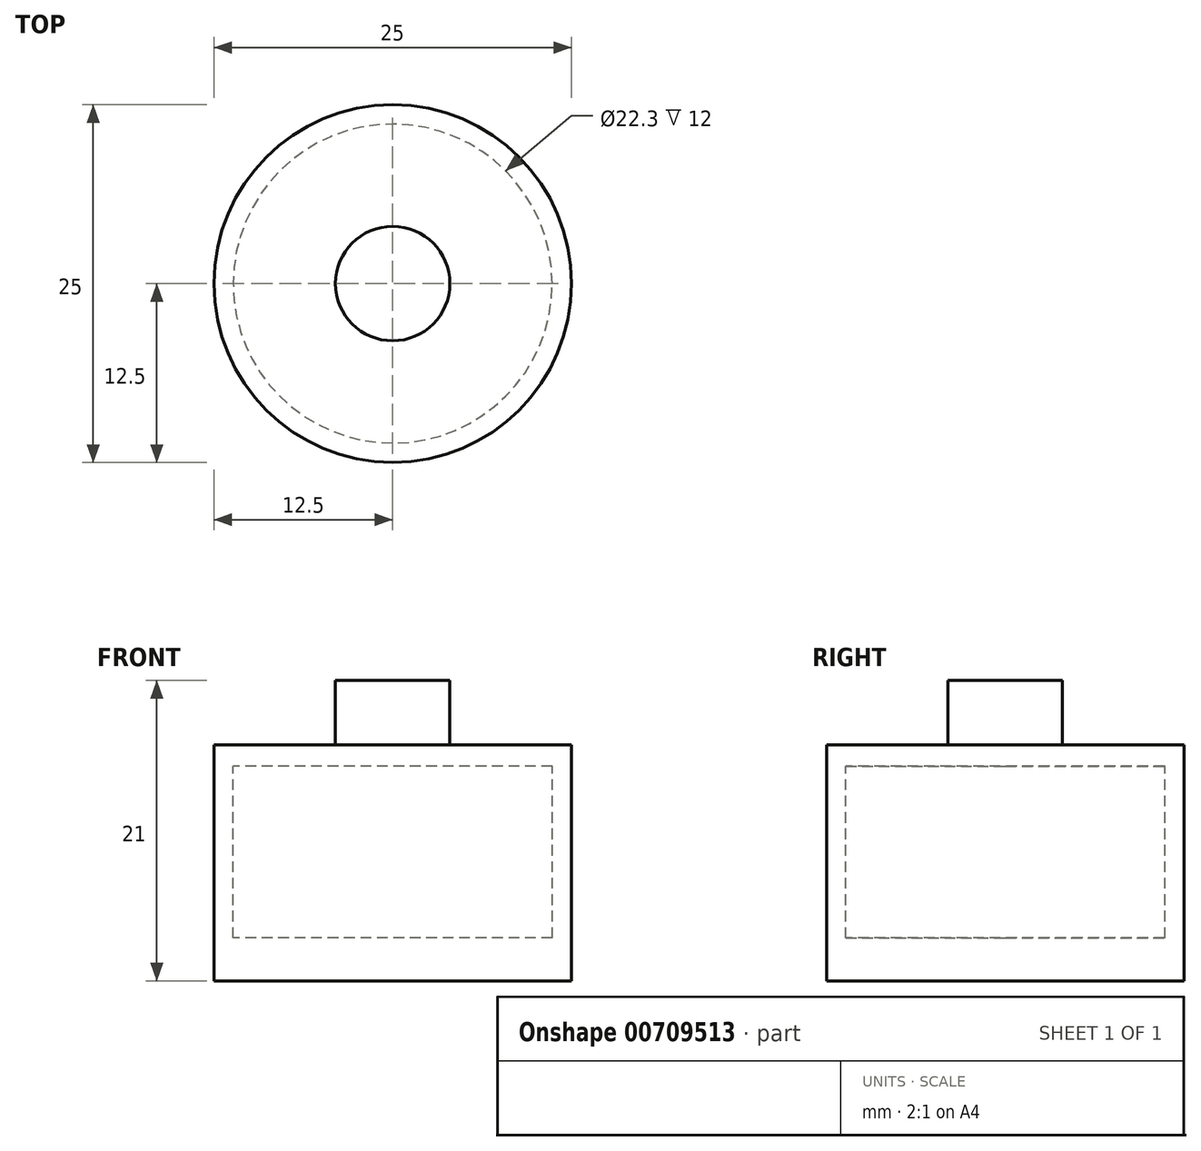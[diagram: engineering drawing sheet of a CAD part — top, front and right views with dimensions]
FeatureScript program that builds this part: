
annotation { "Feature Type Name" : "Feature", "Feature Type Description" : "" }
export const myFeature = defineFeature(function(context is Context, id is Id, definition is map)
    precondition{}
    {
        {
            var Q0;
            Q0=qCreatedBy(makeId("Top.planeOp"),FACE);
            var sketch = newSketch(context, id + "F0", { "sketchPlane" : qUnion([Q0])});
            skCircle(sketch, "E0", {"center": v(0, 0) * mm, "radius": 11.15 * mm});
            skCircle(sketch, "E1", {"center": v(0, 0) * mm, "radius": 4 * mm});
            skCircle(sketch, "E2", {"center": v(0, 0) * mm, "radius": 12.5 * mm});
            skCircle(sketch, "E3", {"center": v(0, 0) * mm, "radius": 8.5 * mm});
            skSolve(sketch);
        }
        {
            var Q0;
            Q0=makeQuery(id+"F0.imprint","IMPRINT",FACE,{"disambiguationData":[TD([[makeQuery(id+"F0.imprint","IMPRINT",EDGE,{"derivedFrom":sQuery(id+"F0.wireOp",EDGE,"E1")}),-1.0]])]});
            extrude(context, id + "F1", {"entities" : qUnion([Q0]), "depth" : 1.5 * mm, "offsetDistance" : 25 * mm});
        }
        {
            var Q0;
            Q0=makeQuery(id+"F0.imprint","IMPRINT",FACE,{"disambiguationData":[TD([[makeQuery(id+"F0.imprint","IMPRINT",EDGE,{"derivedFrom":sQuery(id+"F0.wireOp",EDGE,"E1")}),1.0]])]});
            extrude(context, id + "F2", {"entities" : qUnion([Q0]), "operationType" : NewBodyOperationType.ADD, "depth" : 6 * mm, "offsetDistance" : 25 * mm});
        }
        {
            var Q0;
            Q0=makeQuery(id+"F0.imprint","IMPRINT",FACE,{"disambiguationData":[TD([[makeQuery(id+"F0.imprint","IMPRINT",EDGE,{"derivedFrom":sQuery(id+"F0.wireOp",EDGE,"E0")}),1.0]])]});
            var Q1;
            Q1=makeQuery(id+"F0.imprint","IMPRINT",FACE,{"disambiguationData":[TD([[makeQuery(id+"F0.imprint","IMPRINT",EDGE,{"derivedFrom":sQuery(id+"F0.wireOp",EDGE,"E0")}),-1.0]])]});
            extrude(context, id + "F3", {"entities" : qUnion([Q0, Q1]), "operationType" : NewBodyOperationType.ADD, "depth" : 1.5 * mm, "offsetDistance" : 25 * mm});
        }
        {
            var Q0;
            Q0=makeQuery(id+"F0.imprint","IMPRINT",FACE,{"disambiguationData":[TD([[makeQuery(id+"F0.imprint","IMPRINT",EDGE,{"derivedFrom":sQuery(id+"F0.wireOp",EDGE,"E0")}),-1.0]])]});
            extrude(context, id + "F4", {"entities" : qUnion([Q0]), "operationType" : NewBodyOperationType.ADD, "oppositeDirection" : true, "depth" : 12 * mm, "offsetDistance" : 25 * mm});
        }
        {
            var Q0;
            Q0=makeQuery(id+"F4.opExtrude","CAP_FACE",FACE,{"disambiguationData":[OSD([sQuery(id+"F0.wireOp",EDGE,"E0"),sQuery(id+"F0.wireOp",EDGE,"E2")])],"isStart":false});
            var sketch = newSketch(context, id + "F5", { "sketchPlane" : qUnion([Q0])});
            skCircle(sketch, "E4", {"center": v(0, 0) * mm, "radius": 12.5 * mm});
            skSolve(sketch);
        }
        {
            var Q0;
            Q0 = qSketchRegion(id + "F5", true);
            extrude(context, id + "F6", {"entities" : qUnion([Q0]), "operationType" : NewBodyOperationType.ADD, "depth" : 3 * mm, "offsetDistance" : 25 * mm});
        }
    });
